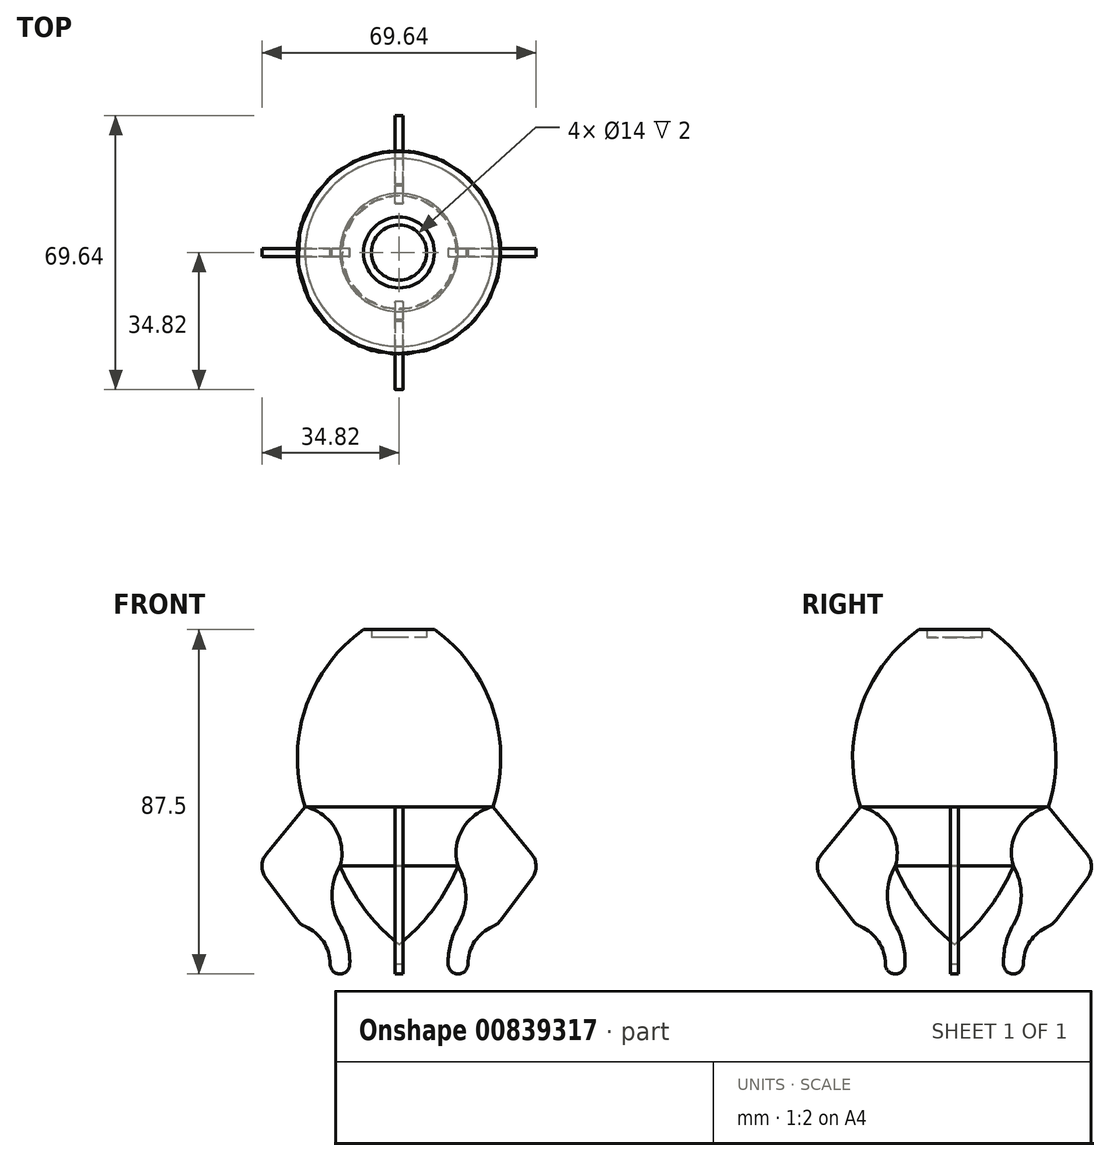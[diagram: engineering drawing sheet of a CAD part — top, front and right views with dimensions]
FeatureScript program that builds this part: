
annotation { "Feature Type Name" : "Feature", "Feature Type Description" : "" }
export const myFeature = defineFeature(function(context is Context, id is Id, definition is map)
    precondition{}
    {
        {
            var Q0;
            Q0=qCreatedBy(makeId("Front.planeOp"),FACE);
            var sketch = newSketch(context, id + "F0", { "sketchPlane" : qUnion([Q0])});
            skLineSegment(sketch, "E0", {"start": v(0, 0) * mm, "end": v(0, 80) * mm});
            skLineSegment(sketch, "E1", {"start": v(0, 80) * mm, "end": v(9, 80) * mm});
            skLineSegment(sketch, "E2", {"start": v(0, 20) * mm, "end": v(15, 20) * mm});
            skLineSegment(sketch, "E3", {"start": v(0, 35) * mm, "end": v(23.88, 35) * mm});
            skArc(sketch, "E4", {"start": v(23.88, 35) * mm, "mid": v(23.82, 59.94) * mm, "end": v(9, 80) * mm});
            skArc(sketch, "E5", {"start": v(23.88, 35) * mm, "mid": v(16.21, 29.41) * mm, "end": v(15, 20) * mm});
            skArc(sketch, "E6", {"start": v(0, 0) * mm, "mid": v(8.77, 9.05) * mm, "end": v(15, 20) * mm});
            skLineSegment(sketch, "E7", {"start": v(0, 80) * mm, "end": v(0, 78) * mm});
            skLineSegment(sketch, "E8", {"start": v(0, 78) * mm, "end": v(7, 78) * mm});
            skLineSegment(sketch, "E9", {"start": v(7, 80) * mm, "end": v(7, 78) * mm});
            skSolve(sketch);
        }
        {
            var Q0;
            {var subQ0=sQuery(id+"F0.wireOp",EDGE,"E3");Q0=makeQuery(id+"F0.imprint","IMPRINT",FACE,{"disambiguationData":[TD([[makeQuery(id+"F0.imprint","IMPRINT",EDGE,{"derivedFrom":subQ0}),1.0]])]});}
            var Q1;
            {var subQ0=sQuery(id+"F0.wireOp",EDGE,"E2");Q1=makeQuery(id+"F0.imprint","IMPRINT",FACE,{"disambiguationData":[TD([[makeQuery(id+"F0.imprint","IMPRINT",EDGE,{"derivedFrom":subQ0}),1.0]])]});}
            var Q2;
            {var subQ2=sQuery(id+"F0.wireOp",EDGE,"E2");Q2=makeQuery(id+"F0.imprint","IMPRINT",FACE,{"disambiguationData":[TD([[makeQuery(id+"F0.imprint","IMPRINT",EDGE,{"derivedFrom":subQ2}),-1.0]])]});}
            var Q3;
            Q3=sQuery(id+"F0.wireOp",EDGE,"E0");
            revolve(context, id + "F1", {"surfaceOperationType" : NewSurfaceOperationType.NEW, "entities" : qUnion([Q0, Q1, Q2]), "axis" : qUnion([Q3]), "revolveType" : RevolveType.FULL});
        }
        {
            var Q0;
            Q0=qCreatedBy(makeId("Front.planeOp"),FACE);
            var sketch = newSketch(context, id + "F2", { "sketchPlane" : qUnion([Q0])});
            skLineSegment(sketch, "E10.0", {"start": v(23.88, 35) * mm, "end": v(-23.88, 35) * mm});
            skLineSegment(sketch, "E11.0", {"start": v(15, 20) * mm, "end": v(-15, 20) * mm});
            skLineSegment(sketch, "E12", {"start": v(-23.88, 35) * mm, "end": v(-15, 20) * mm});
            skLineSegment(sketch, "E13", {"start": v(0, 35) * mm, "end": v(0, 20) * mm});
            skSolve(sketch);
        }
        {
            var Q0;
            Q0 = qSketchRegion(id + "F2", true);
            extrude(context, id + "F3", {"entities" : qUnion([Q0]), "operationType" : NewBodyOperationType.ADD, "endBound" : BoundingType.SYMMETRIC, "depth" : 2 * mm, "offsetDistance" : 25 * mm});
        }
        {
            var Q0;
            Q0=qCreatedBy(makeId("Front.planeOp"),FACE);
            var sketch = newSketch(context, id + "F4", { "sketchPlane" : qUnion([Q0])});
            skLineSegment(sketch, "E14", {"start": v(0, 0) * mm, "end": v(0, -5) * mm});
            skLineSegment(sketch, "E15", {"start": v(0, -5) * mm, "end": v(-15, -5) * mm});
            skLineSegment(sketch, "E16", {"start": v(-15, -5) * mm, "end": v(-15, 5) * mm});
            skLineSegment(sketch, "E17", {"start": v(-15, 5) * mm, "end": v(-25, 5) * mm});
            skLineSegment(sketch, "E18", {"start": v(-15.08, -5) * mm, "end": v(-15.08, -5) * mm});
            skLineSegment(sketch, "E19", {"start": v(-15, -5) * mm, "end": v(-15.08, -5) * mm});
            skFitSpline(sketch, "E20.0", {"points": [v(-23.86, 35) * mm, v(-23.46, 34.91) * mm, v(-22.67, 34.69) * mm, v(-21.54, 34.24) * mm, v(-20.46, 33.68) * mm, v(-19.6, 33.13) * mm, v(-18.96, 32.63) * mm, v(-18.34, 32.1) * mm, v(-17.62, 31.39) * mm, v(-16.85, 30.45) * mm, v(-16.16, 29.42) * mm, v(-15.6, 28.35) * mm, v(-15.22, 27.4) * mm, v(-14.97, 26.63) * mm, v(-14.76, 25.84) * mm, v(-14.62, 25.04) * mm, v(-14.53, 24.22) * mm, v(-14.5, 23.4) * mm, v(-14.53, 21.98) * mm, v(-14.74, 20.79) * mm, v(-14.97, 20) * mm]});
            skArc(sketch, "E21", {"start": v(-14.97, 20) * mm, "mid": v(-17, 12.5) * mm, "end": v(-15, 5) * mm});
            skArc(sketch, "E22", {"start": v(-17.5, -5) * mm, "mid": v(-15, -7.5) * mm, "end": v(-12.5, -5) * mm});
            skLineSegment(sketch, "E23", {"start": v(-15, -5) * mm, "end": v(-17.5, -5) * mm});
            skArc(sketch, "E24", {"start": v(-12.5, -5) * mm, "mid": v(-13.05, 0.17) * mm, "end": v(-15, 5) * mm});
            skArc(sketch, "E25", {"start": v(-17.5, -5) * mm, "mid": v(-19.23, 0.75) * mm, "end": v(-23.84, 4.59) * mm});
            skLineSegment(sketch, "E26", {"start": v(-23.86, 35) * mm, "end": v(-33.69, 23.02) * mm});
            skLineSegment(sketch, "E27", {"start": v(-33.83, 16.86) * mm, "end": v(-25.9, 6.2) * mm});
            skPoint(sketch, "E28.visualSharp", {"position": v(-36.17, 20) * mm});
            skArc(sketch, "E28.filletArc", {"start": v(-33.69, 23.02) * mm, "mid": v(-34.82, 19.97) * mm, "end": v(-33.83, 16.86) * mm});
            skPoint(sketch, "E29.visualSharp", {"position": v(-25, 5) * mm});
            skArc(sketch, "E29.filletArc", {"start": v(-25.9, 6.2) * mm, "mid": v(-24.97, 5.26) * mm, "end": v(-23.84, 4.59) * mm});
            skSolve(sketch);
        }
        {
            var Q0;
            Q0 = qSketchRegion(id + "F4", true);
            extrude(context, id + "F5", {"entities" : qUnion([Q0]), "operationType" : NewBodyOperationType.ADD, "endBound" : BoundingType.SYMMETRIC, "depth" : 2 * mm, "offsetDistance" : 25 * mm});
        }
        {
            var Q0;
            Q0=makeQuery(id+"F1.opRevolve","SWEPT_BODY",BODY,{"disambiguationData":[OSD([sQuery(id+"F0.wireOp",EDGE,"E0"),sQuery(id+"F0.wireOp",EDGE,"E1"),sQuery(id+"F0.wireOp",EDGE,"E4"),sQuery(id+"F0.wireOp",EDGE,"E5"),sQuery(id+"F0.wireOp",EDGE,"E6"),sQuery(id+"F0.wireOp",EDGE,"E8"),sQuery(id+"F0.wireOp",EDGE,"E9")])]});
            var Q1;
            Q1=makeQuery(id+"F1.opRevolve","SWEPT_FACE",FACE,{"disambiguationData":[OSD([sQuery(id+"F0.wireOp",EDGE,"E4")])]});
            circularPattern(context, id + "F6", {"entities" : qUnion([Q0]), "axis" : qUnion([Q1]), "angle" : 360 * degree, "instanceCount" : 4, "equalSpace" : true});
        }
    });
